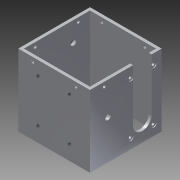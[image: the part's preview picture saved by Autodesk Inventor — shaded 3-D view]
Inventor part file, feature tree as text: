
AUTODESK INVENTOR PART (.ipt)
format: ipt  version: 2013 (Build 170138000, 138)  size: 201,216 bytes
history: native  units: mm
features: sketch x6, hole x5, thread x4, other x1, extrude x1
ambient origin geometry x1: Origin
feature tree (17):
  other  "ソリッド1"
  extrude  "押し出し1"  Depth=50.0mm
  hole  "穴1"  [1 undecoded]
  hole  "穴6"  [1 undecoded]
  hole  "穴13"  [1 undecoded]
  thread  "ねじ13"
  thread  "ねじ14"
  thread  "ねじ15"
  thread  "ねじ16"
  hole  "穴14"  [1 undecoded]
  hole  "穴15"  [1 undecoded]
  sketch  "スケッチ1"
  sketch  "スケッチ3"
  sketch  "スケッチ11"
  sketch  "スケッチ18"
  sketch  "スケッチ19"
  sketch  "スケッチ20"
note: 5 required parameter values undecoded (feature->parameter linkage not recoverable at this tier; creation-order binding heuristic only, values carry confidence <= 0.55)
